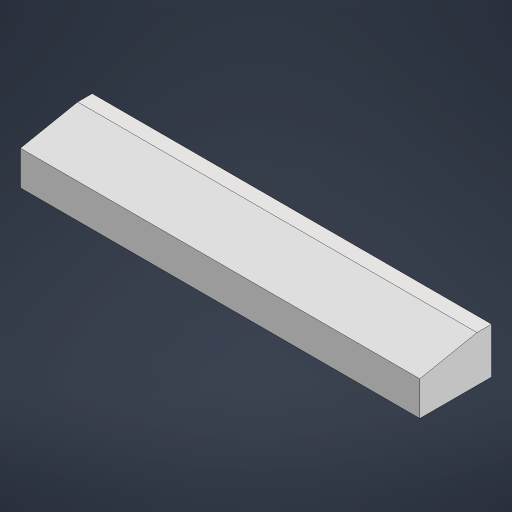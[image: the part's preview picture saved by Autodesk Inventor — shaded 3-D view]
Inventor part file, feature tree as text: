
AUTODESK INVENTOR PART (.ipt)
format: ipt  version: 2023.1 (Build 271208000, 208)  size: 157,696 bytes
history: native  units: in
note: dims shown in document units (in); Inventor stores cm internally (conversion verified against a paired STEP export)
features: extrude x1, sketch x1
ambient origin geometry x8: Origin, YZ Plane, XZ Plane, XY Plane, X Axis, Y Axis, Z Axis, Center Point
bodies: Solid1 (feature_tree)
feature tree (2):
  extrude  "Extrusion1"  Depth=5.5in
  sketch  "Sketch2"  dims[d3=8.625in d4=5.5in d5=1.75in d6=1.375in d7=4.125in d8=48.0in d9=0.0in]
